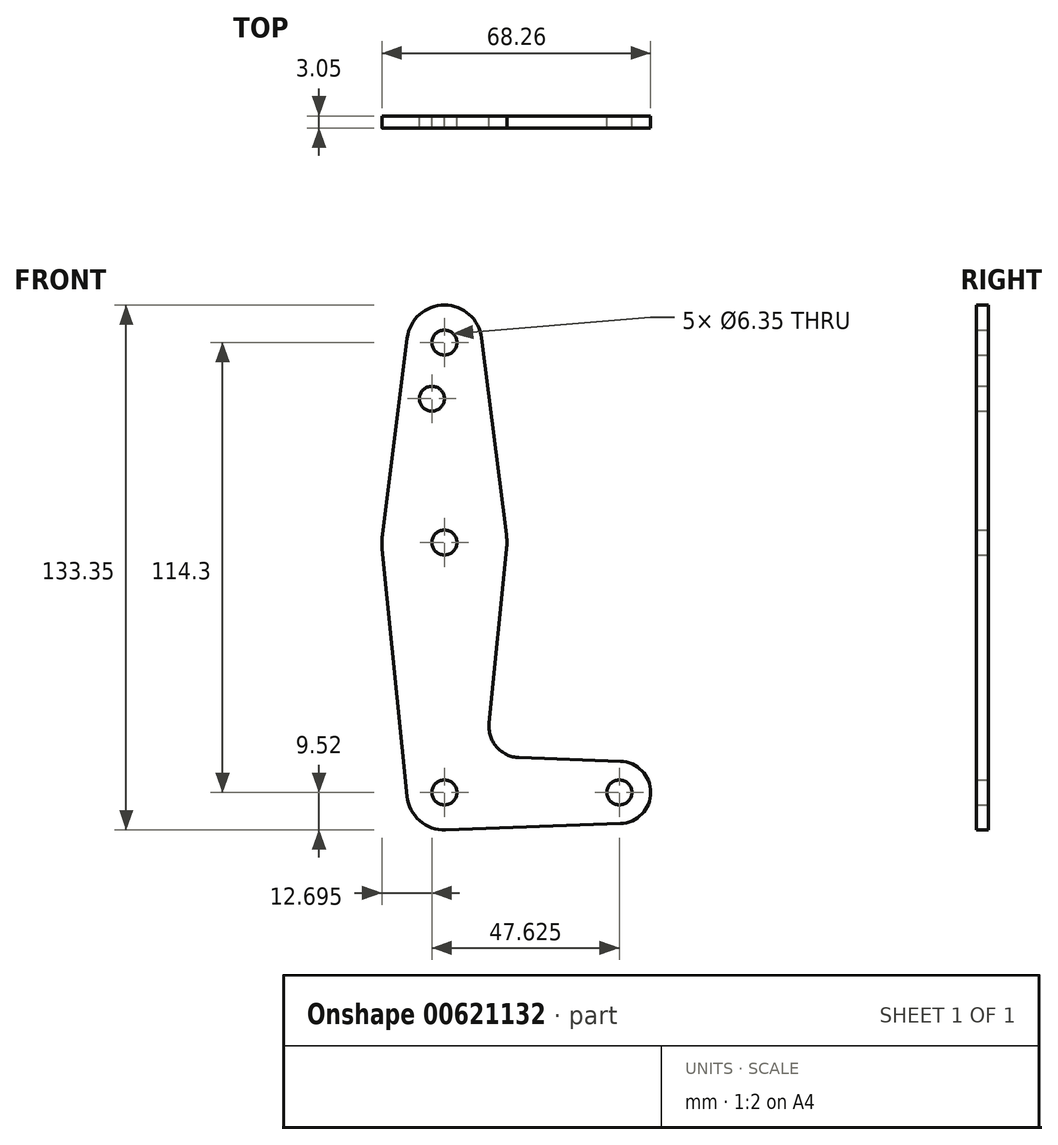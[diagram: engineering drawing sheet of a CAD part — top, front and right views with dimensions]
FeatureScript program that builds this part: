
annotation { "Feature Type Name" : "Feature", "Feature Type Description" : "" }
export const myFeature = defineFeature(function(context is Context, id is Id, definition is map)
    precondition{}
    {
        {
            var Q0;
            Q0=qCreatedBy(makeId("Front.planeOp"),FACE);
            var sketch = newSketch(context, id + "F0", { "sketchPlane" : qUnion([Q0])});
            skLineSegment(sketch, "E0", {"start": v(0, 0) * mm, "end": v(0, 114.3) * mm, "construction": true});
            skLineSegment(sketch, "E1", {"start": v(0, 0) * mm, "end": v(44.45, 0) * mm, "construction": true});
            skCircle(sketch, "E2", {"center": v(0, 0) * mm, "radius": 9.52 * mm});
            skCircle(sketch, "E3", {"center": v(44.45, 0) * mm, "radius": 7.94 * mm});
            skCircle(sketch, "E4", {"center": v(0, 114.3) * mm, "radius": 9.53 * mm});
            skCircle(sketch, "E5", {"center": v(0, 63.5) * mm, "radius": 15.88 * mm});
            skLineSegment(sketch, "E6", {"start": v(-9.45, 115.5) * mm, "end": v(-15.75, 65.48) * mm});
            skLineSegment(sketch, "E7", {"start": v(0.34, -9.52) * mm, "end": v(44.73, -7.93) * mm});
            skCircle(sketch, "E8", {"center": v(0, 63.5) * mm, "radius": 3.17 * mm});
            skCircle(sketch, "E9", {"center": v(0, 0) * mm, "radius": 3.18 * mm});
            skCircle(sketch, "E10", {"center": v(44.45, 0) * mm, "radius": 3.18 * mm});
            skCircle(sketch, "E11", {"center": v(-3.18, 100.03) * mm, "radius": 3.18 * mm});
            skPoint(sketch, "E12.newPointA", {"position": v(0.34, 9.52) * mm});
            skPoint(sketch, "E12.newPointB", {"position": v(9.48, -0.9) * mm});
            skLineSegment(sketch, "E13", {"start": v(-9.48, -0.95) * mm, "end": v(-15.8, 61.91) * mm});
            skLineSegment(sketch, "E14.MirrorCS", {"start": v(9.45, 115.5) * mm, "end": v(15.75, 65.48) * mm});
            skLineSegment(sketch, "E15.MirrorCS", {"start": v(11.34, 17.6) * mm, "end": v(15.8, 61.91) * mm});
            skLineSegment(sketch, "E16.MirrorCS", {"start": v(18.97, 8.85) * mm, "end": v(44.73, 7.93) * mm});
            skCircle(sketch, "E17", {"center": v(0, 114.3) * mm, "radius": 3.18 * mm});
            skPoint(sketch, "E18.newPointA", {"position": v(9.48, -0.95) * mm});
            skArc(sketch, "E18.filletArc", {"start": v(11.34, 17.6) * mm, "mid": v(13.26, 11.57) * mm, "end": v(18.97, 8.85) * mm});
            skSolve(sketch);
        }
        {
            var Q0;
            Q0=makeQuery(id+"F0.imprint","IMPRINT",FACE,{"disambiguationData":[TD([[makeQuery(id+"F0.imprint","IMPRINT",EDGE,{"derivedFrom":sQuery(id+"F0.wireOp",EDGE,"E17")}),-1.0]])]});
            var Q1;
            {var subQ0=sQuery(id+"F0.wireOp",EDGE,"E6");Q1=makeQuery(id+"F0.imprint","IMPRINT",FACE,{"disambiguationData":[TD([[makeQuery(id+"F0.imprint","IMPRINT",EDGE,{"derivedFrom":subQ0}),1.0]])]});}
            var Q2;
            Q2=makeQuery(id+"F0.imprint","IMPRINT",FACE,{"disambiguationData":[TD([[makeQuery(id+"F0.imprint","IMPRINT",EDGE,{"derivedFrom":sQuery(id+"F0.wireOp",EDGE,"E8")}),-1.0]])]});
            var Q3;
            {var subQ4=sQuery(id+"F0.wireOp",EDGE,"E7");Q3=makeQuery(id+"F0.imprint","IMPRINT",FACE,{"disambiguationData":[TD([[makeQuery(id+"F0.imprint","IMPRINT",EDGE,{"derivedFrom":subQ4}),1.0]])]});}
            var Q4;
            Q4=makeQuery(id+"F0.imprint","IMPRINT",FACE,{"disambiguationData":[TD([[makeQuery(id+"F0.imprint","IMPRINT",EDGE,{"derivedFrom":sQuery(id+"F0.wireOp",EDGE,"E9")}),-1.0]])]});
            var Q5;
            Q5=makeQuery(id+"F0.imprint","IMPRINT",FACE,{"disambiguationData":[TD([[makeQuery(id+"F0.imprint","IMPRINT",EDGE,{"derivedFrom":sQuery(id+"F0.wireOp",EDGE,"E10")}),-1.0]])]});
            extrude(context, id + "F1", {"entities" : qUnion([Q0, Q1, Q2, Q3, Q4, Q5]), "depth" : 3.05 * mm, "offsetDistance" : 25.4 * mm});
        }
    });
